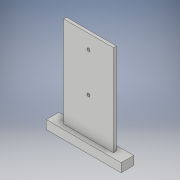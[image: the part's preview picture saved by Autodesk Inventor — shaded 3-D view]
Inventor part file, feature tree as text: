
AUTODESK INVENTOR PART (.ipt)
format: ipt  version: 2017 (Build 210142000, 142)  size: 129,536 bytes
history: native  units: in
note: dims shown in document units (in); Inventor stores cm internally (conversion verified against a paired STEP export)
features: extrude x2, sketch x2
ambient origin geometry x8: Origin, YZ Plane, XZ Plane, XY Plane, X Axis, Y Axis, Z Axis, Center Point
bodies: Solid1 (feature_tree)
feature tree (4):
  extrude  "Extrusion1"  Depth=0.1181in TaperAngle=0.0deg
  extrude  "Extrusion2"  Depth=3.0in TaperAngle=0.0deg
  sketch  "Sketch1"  dims[d0=1.575in d1=0.6in d2=2.4in d3=0.122in d4=0.122in d5=0.57in d6=1.0in d7=1.0in d8=4.0in d9=0.5in d10=0.5in d11=0.35in d12=0.1181in d13=0.0in]
  sketch  "Sketch2"  dims[d15=0.35in d17=3.0in d18=0.0in d19=0.1931in d20=0.193in]
